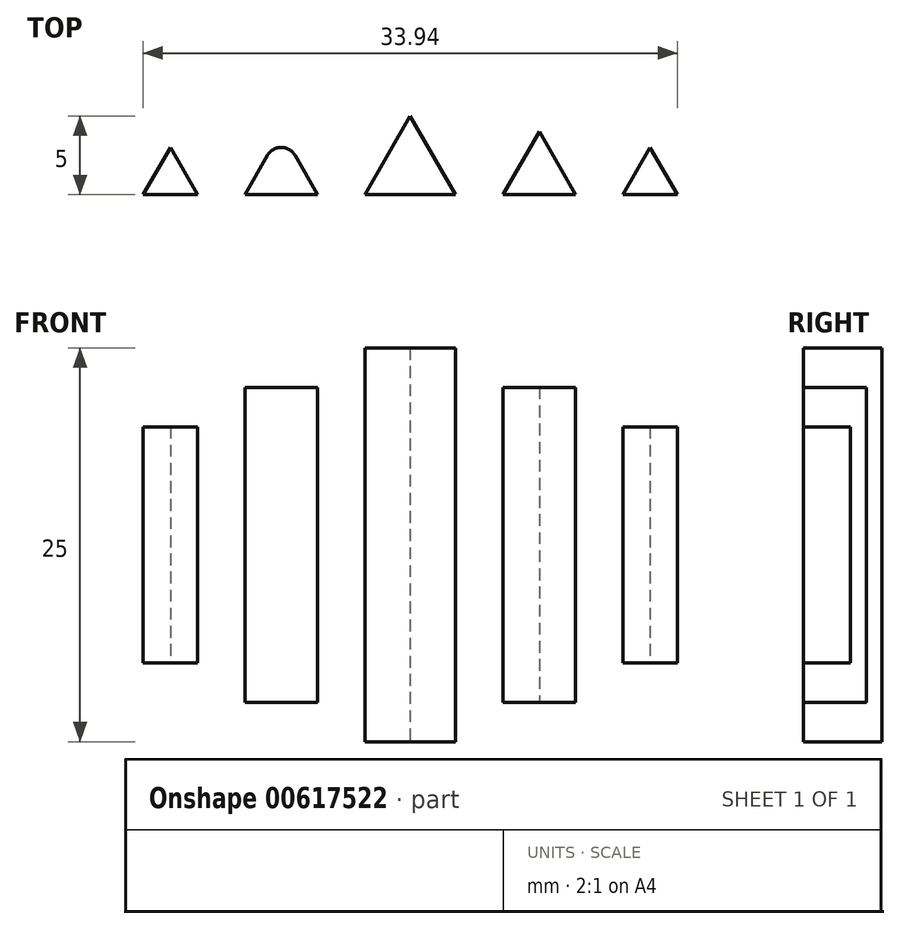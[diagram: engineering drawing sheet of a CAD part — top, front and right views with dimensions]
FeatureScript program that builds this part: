
annotation { "Feature Type Name" : "Feature", "Feature Type Description" : "" }
export const myFeature = defineFeature(function(context is Context, id is Id, definition is map)
    precondition{}
    {
        {
            var Q0;
            Q0=qCreatedBy(makeId("Top.planeOp"),FACE);
            var sketch = newSketch(context, id + "F0", { "sketchPlane" : qUnion([Q0])});
            skCircle(sketch, "E0.cCircle", {"center": v(0, 1.67) * mm, "radius": 1.67 * mm, "construction": true});
            skLineSegment(sketch, "E0.0", {"start": v(2.89, 0) * mm, "end": v(-2.89, 0) * mm});
            skLineSegment(sketch, "E0.1", {"start": v(-2.89, 0) * mm, "end": v(0, 5) * mm});
            skLineSegment(sketch, "E0.2", {"start": v(0, 5) * mm, "end": v(2.89, 0) * mm});
            skPoint(sketch, "E0.0.midPoint", {"position": v(0, 0) * mm});
            skCircle(sketch, "E1.cCircle", {"center": v(-8.2, 1.33) * mm, "radius": 1.33 * mm, "construction": true});
            skLineSegment(sketch, "E1.0", {"start": v(-5.89, 0) * mm, "end": v(-10.5, 0) * mm});
            skLineSegment(sketch, "E1.1", {"start": v(-10.5, 0) * mm, "end": v(-8.2, 4) * mm});
            skLineSegment(sketch, "E1.2", {"start": v(-8.2, 4) * mm, "end": v(-5.89, 0) * mm});
            skPoint(sketch, "E1.0.midPoint", {"position": v(-8.2, 0) * mm});
            skCircle(sketch, "E2.cCircle", {"center": v(-15.24, 1) * mm, "radius": 1 * mm, "construction": true});
            skLineSegment(sketch, "E2.0", {"start": v(-13.5, 0) * mm, "end": v(-16.97, 0) * mm});
            skLineSegment(sketch, "E2.1", {"start": v(-16.97, 0) * mm, "end": v(-15.24, 3) * mm});
            skLineSegment(sketch, "E2.2", {"start": v(-15.24, 3) * mm, "end": v(-13.5, 0) * mm});
            skPoint(sketch, "E2.0.midPoint", {"position": v(-15.24, 0) * mm});
            skLineSegment(sketch, "E3", {"start": v(-5.89, 0) * mm, "end": v(-2.89, 0) * mm});
            skLineSegment(sketch, "E4", {"start": v(-13.5, 0) * mm, "end": v(-10.5, 0) * mm});
            skSolve(sketch);
        }
        {
            var Q0;
            Q0=makeQuery(id+"F0.imprint","IMPRINT",FACE,{"disambiguationData":[TD([[makeQuery(id+"F0.imprint","IMPRINT",EDGE,{"derivedFrom":sQuery(id+"F0.wireOp",EDGE,"E0.0")}),-1.0]])]});
            extrude(context, id + "F1", {"entities" : qUnion([Q0]), "endBound" : BoundingType.SYMMETRIC, "depth" : 25 * mm, "offsetDistance" : 25 * mm});
        }
        {
            var Q0;
            Q0=makeQuery(id+"F0.imprint","IMPRINT",FACE,{"disambiguationData":[TD([[makeQuery(id+"F0.imprint","IMPRINT",EDGE,{"derivedFrom":sQuery(id+"F0.wireOp",EDGE,"E1.0")}),-1.0]])]});
            extrude(context, id + "F2", {"entities" : qUnion([Q0]), "endBound" : BoundingType.SYMMETRIC, "depth" : 20 * mm, "offsetDistance" : 25 * mm});
        }
        {
            var Q0;
            Q0=makeQuery(id+"F0.imprint","IMPRINT",FACE,{"disambiguationData":[TD([[makeQuery(id+"F0.imprint","IMPRINT",EDGE,{"derivedFrom":sQuery(id+"F0.wireOp",EDGE,"E2.0")}),-1.0]])]});
            extrude(context, id + "F3", {"entities" : qUnion([Q0]), "endBound" : BoundingType.SYMMETRIC, "depth" : 15 * mm, "offsetDistance" : 25 * mm});
        }
        {
            var Q0;
            Q0=makeQuery(id+"F2.opExtrude","SWEPT_BODY",BODY,{"disambiguationData":[OSD([sQuery(id+"F0.wireOp",EDGE,"E1.0"),sQuery(id+"F0.wireOp",EDGE,"E1.1"),sQuery(id+"F0.wireOp",EDGE,"E1.2")])]});
            var Q1;
            Q1=makeQuery(id+"F3.opExtrude","SWEPT_BODY",BODY,{"disambiguationData":[OSD([sQuery(id+"F0.wireOp",EDGE,"E2.0"),sQuery(id+"F0.wireOp",EDGE,"E2.1"),sQuery(id+"F0.wireOp",EDGE,"E2.2")])]});
            var Q2;
            Q2=qCreatedBy(makeId("Right.planeOp"),FACE);
            mirror(context, id + "F4", {"entities" : qUnion([Q0, Q1]), "mirrorPlane" : qUnion([Q2])});
        }
        {
            var Q0;
            Q0=sQuery(id+"F0.wireOp",EDGE,"E4");
            extrude(context, id + "F5", {"bodyType" : ToolBodyType.SURFACE, "surfaceEntities" : qUnion([Q0]), "endBound" : BoundingType.SYMMETRIC, "oppositeDirection" : true, "depth" : 15 * mm, "offsetDistance" : 25 * mm});
        }
        {
            var Q0;
            Q0=sQuery(id+"F0.wireOp",EDGE,"E3");
            extrude(context, id + "F6", {"bodyType" : ToolBodyType.SURFACE, "surfaceEntities" : qUnion([Q0]), "endBound" : BoundingType.SYMMETRIC, "depth" : 20 * mm, "offsetDistance" : 25 * mm});
        }
        {
            var Q0;
            Q0=makeQuery(id+"F2.opExtrude","SWEPT_EDGE",EDGE,{"disambiguationData":[OSD([sQuery(id+"F0.wireOp",EDGE,"E1.1"),sQuery(id+"F0.wireOp",EDGE,"E1.2")])]});
            fillet(context, id + "F7", {"entities" : qUnion([Q0]), "radius" : 1 * mm, "tangentPropagation" : true, "allowEdgeOverflow" : false});
        }
    });
